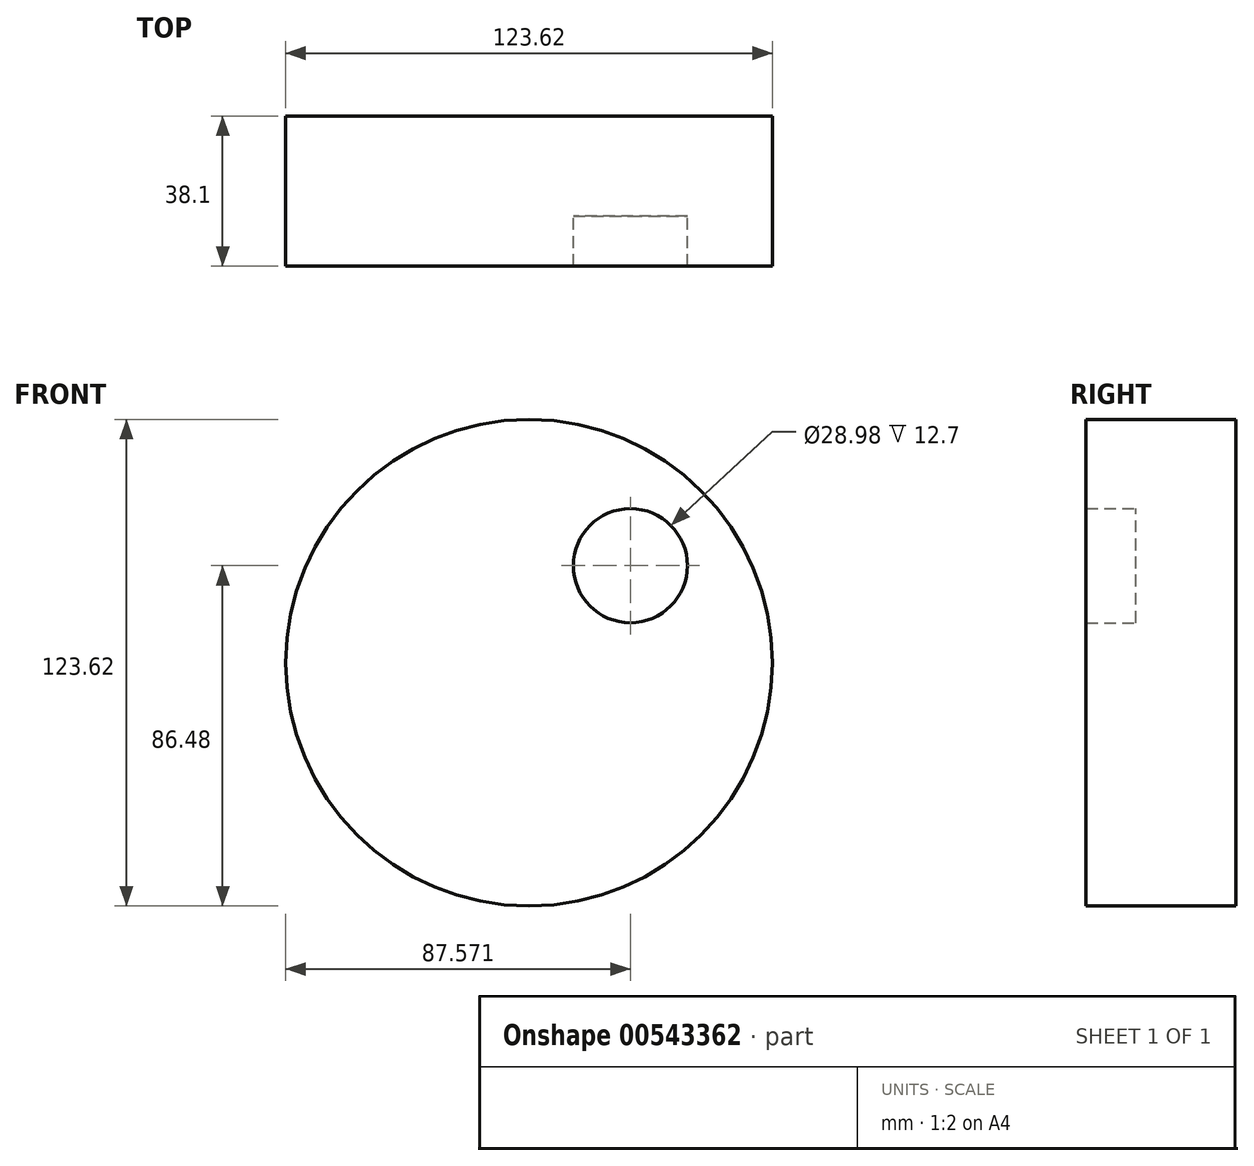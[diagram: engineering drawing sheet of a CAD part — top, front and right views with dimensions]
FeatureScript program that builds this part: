
annotation { "Feature Type Name" : "Feature", "Feature Type Description" : "" }
export const myFeature = defineFeature(function(context is Context, id is Id, definition is map)
    precondition{}
    {
        {
            var Q0;
            Q0=qCreatedBy(makeId("Front.planeOp"),FACE);
            var sketch = newSketch(context, id + "F0", { "sketchPlane" : qUnion([Q0])});
            skCircle(sketch, "E0", {"center": v(-0.1, -0.1) * mm, "radius": 61.8 * mm});
            skSolve(sketch);
        }
        {
            var Q0;
            Q0=makeQuery(id+"F0.imprint","IMPRINT",FACE,{"disambiguationData":[TD([[makeQuery(id+"F0.imprint","IMPRINT",EDGE,{"derivedFrom":sQuery(id+"F0.wireOp",EDGE,"E0")}),1.0]])]});
            extrude(context, id + "F1", {"entities" : qUnion([Q0]), "depth" : 25.4 * mm, "offsetDistance" : 25.4 * mm});
        }
        {
            var Q0;
            Q0=makeQuery(id+"F1.opExtrude","CAP_FACE",FACE,{"disambiguationData":[OSD([sQuery(id+"F0.wireOp",EDGE,"E0")])],"isStart":false});
            var sketch = newSketch(context, id + "F2", { "sketchPlane" : qUnion([Q0])});
            skCircle(sketch, "E1", {"center": v(-25.65, 24.56) * mm, "radius": 14.49 * mm});
            skCircle(sketch, "E2.MirrorC", {"center": v(25.65, 24.56) * mm, "radius": 14.49 * mm});
            skSolve(sketch);
        }
        {
            var Q0;
            Q0=makeQuery(id+"F2.imprint","IMPRINT",FACE,{"disambiguationData":[TD([[makeQuery(id+"F2.imprint","IMPRINT",EDGE,{"derivedFrom":sQuery(id+"F2.wireOp",EDGE,"E1")}),1.0]])]});
            var Q1;
            Q1=makeQuery(id+"F2.imprint","IMPRINT",FACE,{"disambiguationData":[TD([[makeQuery(id+"F2.imprint","IMPRINT",EDGE,{"derivedFrom":sQuery(id+"F2.wireOp",EDGE,"E2.MirrorC")}),-1.0]])]});
            extrude(context, id + "F3", {"entities" : qUnion([Q0, Q1]), "operationType" : NewBodyOperationType.ADD, "depth" : 12.7 * mm, "offsetDistance" : 25.4 * mm});
        }
    });
